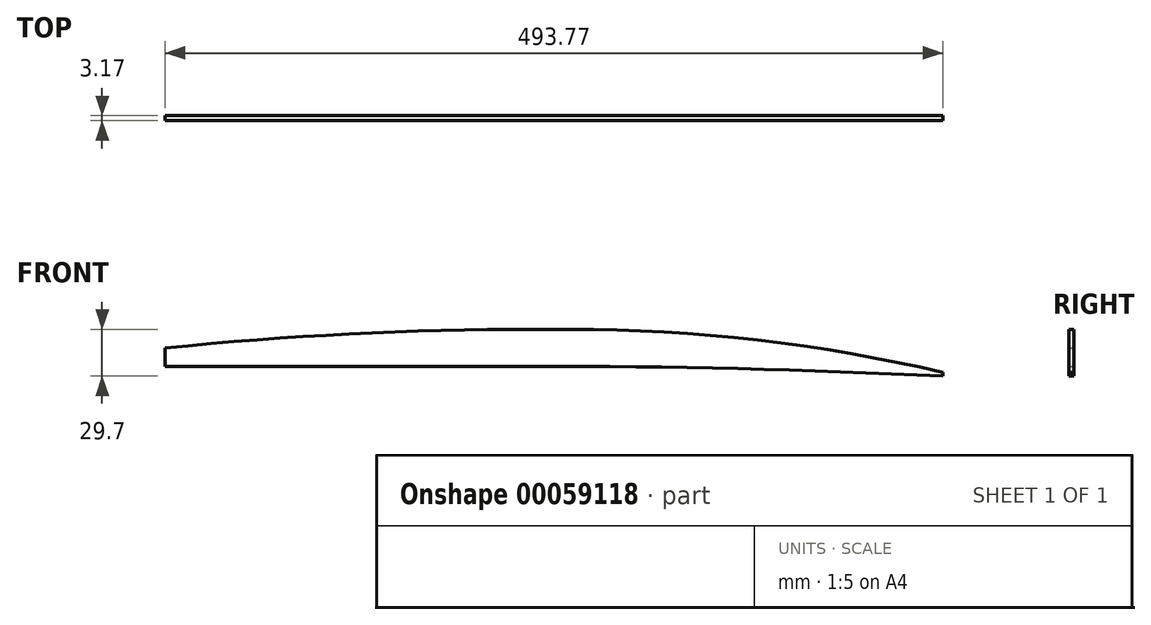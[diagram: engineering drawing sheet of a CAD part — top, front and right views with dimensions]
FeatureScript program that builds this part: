
annotation { "Feature Type Name" : "Feature", "Feature Type Description" : "" }
export const myFeature = defineFeature(function(context is Context, id is Id, definition is map)
    precondition{}
    {
        {
            var Q0;
            Q0=qCreatedBy(makeId("Front.planeOp"),FACE);
            var sketch = newSketch(context, id + "F0", { "sketchPlane" : qUnion([Q0])});
            skLineSegment(sketch, "E0", {"start": v(-232.64, 31.37) * mm, "end": v(0.7, 31.37) * mm, "construction": true});
            skLineSegment(sketch, "E1", {"start": v(-232.64, -46.7) * mm, "end": v(-232.64, 31.37) * mm, "construction": true});
            skLineSegment(sketch, "E2", {"start": v(0.7, -46.7) * mm, "end": v(-232.64, -46.7) * mm, "construction": true});
            skArc(sketch, "E3", {"start": v(246.96, -35.25) * mm, "mid": v(128.26, 14.42) * mm, "end": v(0.7, 31.37) * mm, "construction": true});
            skArc(sketch, "E4", {"start": v(0.7, -46.7) * mm, "mid": v(123.96, -43.83) * mm, "end": v(246.96, -35.25) * mm, "construction": true});
            skLineSegment(sketch, "E5", {"start": v(-232.12, 39.13) * mm, "end": v(250.48, 39.13) * mm, "construction": true});
            skLineSegment(sketch, "E6", {"start": v(-232.64, -62.72) * mm, "end": v(-232.64, -74.32) * mm});
            skLineSegment(sketch, "E7", {"start": v(-232.64, -74.32) * mm, "end": v(1.18, -74.32) * mm});
            skLineSegment(sketch, "E8", {"start": v(1.18, -50.88) * mm, "end": v(24.22, -50.88) * mm});
            skLineSegment(sketch, "E9", {"start": v(261.13, -80.58) * mm, "end": v(261.13, -78.15) * mm});
            skArc(sketch, "E10", {"start": v(1.18, -50.88) * mm, "mid": v(-115.88, -53.84) * mm, "end": v(-232.64, -62.72) * mm});
            skArc(sketch, "E11", {"start": v(261.13, -78.15) * mm, "mid": v(143.46, -57.72) * mm, "end": v(24.22, -50.88) * mm});
            skArc(sketch, "E12", {"start": v(261.13, -80.58) * mm, "mid": v(131.2, -75.86) * mm, "end": v(1.18, -74.32) * mm});
            skSolve(sketch);
        }
        {
            var Q0;
            Q0=qSketchRegion(id+"F0",true);
            extrude(context, id + "F1", {"entities" : qUnion([Q0]), "depth" : 3.17 * mm});
        }
    });
